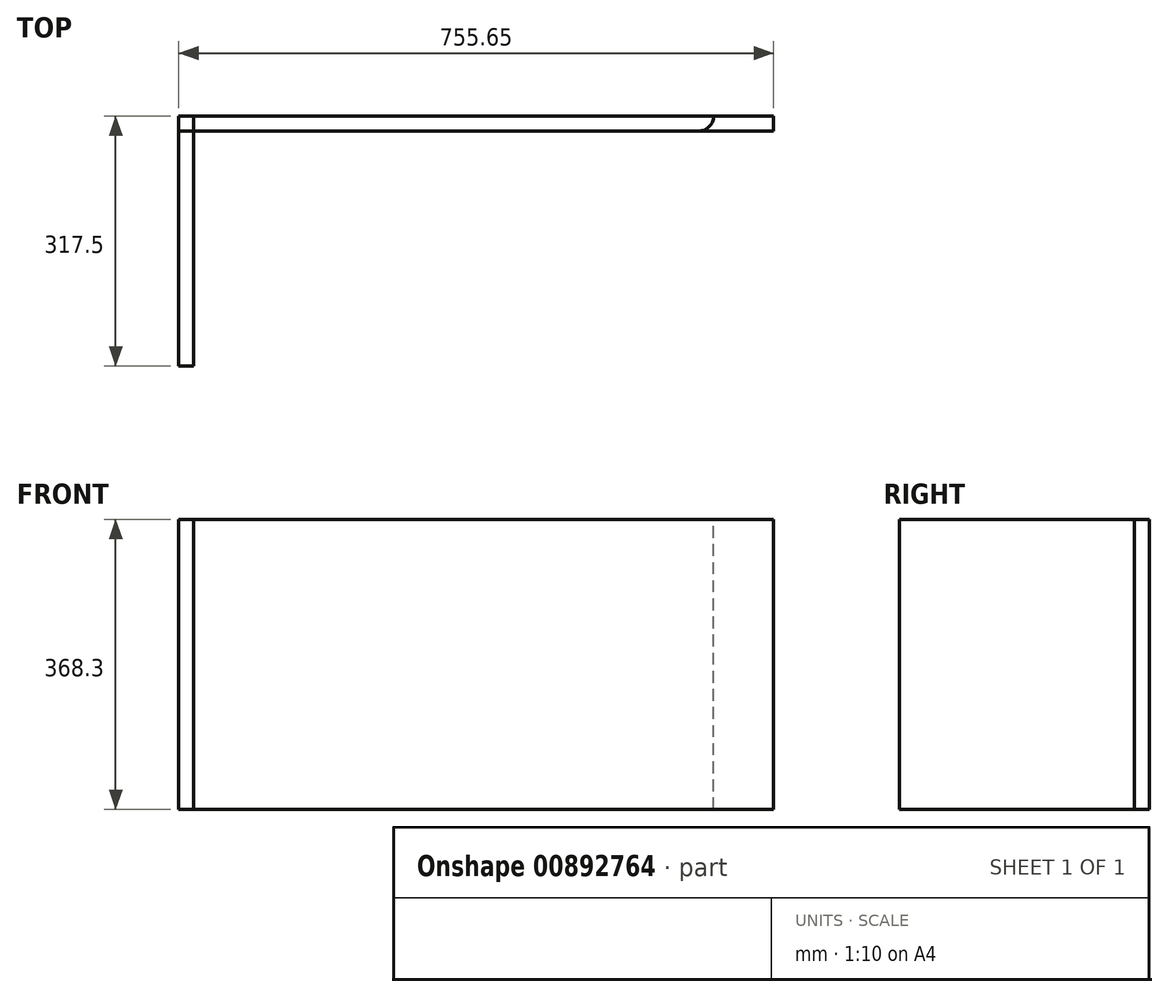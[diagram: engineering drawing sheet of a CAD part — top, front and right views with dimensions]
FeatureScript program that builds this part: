
annotation { "Feature Type Name" : "Feature", "Feature Type Description" : "" }
export const myFeature = defineFeature(function(context is Context, id is Id, definition is map)
    precondition{}
    {
        {
            var Q0;
            Q0=qCreatedBy(makeId("Front.planeOp"),FACE);
            var sketch = newSketch(context, id + "F0", { "sketchPlane" : qUnion([Q0])});
            skLineSegment(sketch, "E0.bottom", {"start": v(0, 0) * mm, "end": v(755.65, 0) * mm});
            skLineSegment(sketch, "E0.top", {"start": v(0, 368.3) * mm, "end": v(755.65, 368.3) * mm});
            skLineSegment(sketch, "E0.left", {"start": v(0, 0) * mm, "end": v(0, 368.3) * mm});
            skLineSegment(sketch, "E0.right", {"start": v(755.65, 0) * mm, "end": v(755.65, 368.3) * mm});
            skSolve(sketch);
        }
        {
            var Q0;
            Q0=makeQuery(id+"F0.imprint","IMPRINT",FACE,{"disambiguationData":[TD([[makeQuery(id+"F0.imprint","IMPRINT",EDGE,{"derivedFrom":sQuery(id+"F0.wireOp",EDGE,"E0.bottom")}),1.0]])]});
            extrude(context, id + "F1", {"entities" : qUnion([Q0]), "depth" : 19.05 * mm, "offsetDistance" : 25.4 * mm});
        }
        {
            var Q0;
            Q0=qCreatedBy(makeId("Front.planeOp"),FACE);
            var sketch = newSketch(context, id + "F2", { "sketchPlane" : qUnion([Q0])});
            skLineSegment(sketch, "E1.bottom", {"start": v(0, 0) * mm, "end": v(679.45, 0) * mm});
            skLineSegment(sketch, "E1.top", {"start": v(0, 368.3) * mm, "end": v(679.45, 368.3) * mm});
            skLineSegment(sketch, "E1.left", {"start": v(0, 0) * mm, "end": v(0, 368.3) * mm});
            skLineSegment(sketch, "E1.right", {"start": v(679.45, 0) * mm, "end": v(679.45, 368.3) * mm});
            skSolve(sketch);
        }
        {
            var Q0;
            Q0=makeQuery(id+"F2.imprint","IMPRINT",FACE,{"disambiguationData":[TD([[makeQuery(id+"F2.imprint","IMPRINT",EDGE,{"derivedFrom":sQuery(id+"F2.wireOp",EDGE,"E1.bottom")}),1.0]])]});
            extrude(context, id + "F3", {"entities" : qUnion([Q0]), "depth" : 19.05 * mm, "offsetDistance" : 25.4 * mm});
        }
        {
            var Q0;
            Q0=makeQuery(id+"F3.opExtrude","CAP_EDGE",EDGE,{"disambiguationData":[OSD([sQuery(id+"F2.wireOp",EDGE,"E1.right")])],"isStart":false});
            fillet(context, id + "F4", {"entities" : qUnion([Q0]), "radius" : 19.05 * mm, "tangentPropagation" : true, "allowEdgeOverflow" : false});
        }
        {
            var Q0;
            Q0=qCreatedBy(makeId("Right.planeOp"),FACE);
            var sketch = newSketch(context, id + "F5", { "sketchPlane" : qUnion([Q0])});
            skLineSegment(sketch, "E2.bottom", {"start": v(0, 0) * mm, "end": v(-317.5, 0) * mm});
            skLineSegment(sketch, "E2.top", {"start": v(0, 368.3) * mm, "end": v(-317.5, 368.3) * mm});
            skLineSegment(sketch, "E2.left", {"start": v(0, 0) * mm, "end": v(0, 368.3) * mm});
            skLineSegment(sketch, "E2.right", {"start": v(-317.5, 0) * mm, "end": v(-317.5, 368.3) * mm});
            skSolve(sketch);
        }
        {
            var Q0;
            Q0=makeQuery(id+"F5.imprint","IMPRINT",FACE,{"disambiguationData":[TD([[makeQuery(id+"F5.imprint","IMPRINT",EDGE,{"derivedFrom":sQuery(id+"F5.wireOp",EDGE,"E2.bottom")}),-1.0]])]});
            extrude(context, id + "F6", {"entities" : qUnion([Q0]), "depth" : 19.05 * mm, "offsetDistance" : 25.4 * mm});
        }
    });
